# Revit family: Hager-Pablo-IP65-Transparent_Door-sistema-NoHosted-IT-it
name_source: partatom
category: Electrical Equipment
units: mm (PartAtom-declared; Revit-internal decimal feet)

## family parameters
Always vertical = Yes
Cut with Voids When Loaded = No
Panel Configuration = Two Columns, Circuits Across
Part Type = Panelboard
Room Calculation Point = No
Round Connector Dimension = Use Diameter
Shared = No
Work Plane-Based = Yes

## types (8) — shared parameters
Default Elevation = 1219 mm
EF000003 - Tipo di montaggio = EV000384 - A parete
EF000007 - colore = EV000270 - grigio
EF000116 - numero RAL = 7035
EF000118 - con piastra di montaggio = No
EF000339 - tipo di copertura = EV004216 - porta
EF001062 - esecuzione EMC = No
EF001088 - possibilità di applicazione = No
EF001134 - barra DIN = Yes
EF001596 - Attacco Lampada = EV000139 - plastica
EF004462 - tipo di chiusura = EV000154 - altri
EF005474 - grado di protezione (IP) = EV006421 - IP65
EF006244 - coperchio/porta trasparente = Yes
EF006306 - con serratura = No
EF009212 - esecuzione coperchio = EV000116 - chiuso
EF015776 - Morsettiera di terra = No
EF015777 - Morsettiera neutra = No
EF015941 - Segnale di passaggio porta = Yes
HG000001 - Numero di colonne = 1
HG000002 - Con porta = Yes
HG000003 - Gamma = Pablo
HG000005 - Spessore = 3 mm  [stored 0.00984252 ft]
HG000006 - Ad incasso = No
HG000009 - Porta doppia a battente = No
HG000010 - Porte asimmetriche = No
HG000011 - File vuote nella parte basse = No
HG000017 - Distanza tra i poli = 18 mm  [stored 0.0590551 ft]
Manufacturer = Hager
Type Comments = Pablo
zero-valued in all types: EF000218 - profondità di incasso, EF000332 - Altezza della parte incassata, EF000846 - larghezza di montaggio, HG000007 - Numero di colonne vuote, HG000008 - Numero di file vuote

## per-type parameters (varying)
| type | EF000008 - Larghezza | EF000040 - Altezza | EF000049 - profondità | EF000266 - numero di file | EF001131 - profondità interna | EF002950 - Numero moduli DIN | HG000004 - Codice produttore | Model |
| A parete IP65 L143 A210 P102 4 Unità di divisione - B06521 | 143 mm | 210 mm | 102 mm | 1 | 102 mm | 4 | B06521 | B06521 |
| A parete IP65 L215 A210 P105 8 Unità di divisione - B06522 | 215 mm | 210 mm | 105 mm | 1 | 105 mm | 8 | B06522 | B06522 |
| A parete IP65 L314 A263 P143 12 Unità di divisione - B06523 | 314 mm | 263 mm | 143 mm | 1 | 143 mm | 12 | B06523 | B06523 |
| A parete IP65 L314 A420 P143 12 Unità di divisione - B06525 | 314 mm | 420 mm  [stored 1.37795 ft] | 143 mm | 2 | 143 mm | 12 | B06525 | B06525 |
| A parete IP65 L426 A288 P148 18 Unità di divisione - B06524 | 426 mm  [stored 1.39764 ft] | 288 mm | 148 mm | 1 | 148 mm | 18 | B06524 | B06524 |
| A parete IP65 L426 A470 P148 19 Unità di divisione - B06526 | 426 mm  [stored 1.39764 ft] | 470 mm | 148 mm | 2 | 148 mm | 19 | B06526 | B06526 |
| A parete IP65 L426 A657 P148 19 Unità di divisione - B06527 | 426 mm  [stored 1.39764 ft] | 657 mm | 148 mm | 3 | 148 mm | 19 | B06527 | B06527 |
| A parete IP65 L426 A903 P168 19 Unità di divisione - B06528 | 426 mm  [stored 1.39764 ft] | 903 mm  [stored 2.9626 ft] | 168 mm  [stored 0.551181 ft] | 4 | 168 mm  [stored 0.551181 ft] | 19 | B06528 | B06528 |

note: [stored X ft] marks values corroborated as IEEE doubles in the binary element streams (Revit-internal decimal feet)

## geometry (parser evidence)
native form markers: Sweep x13
no freeform markers — native parametric forms only
